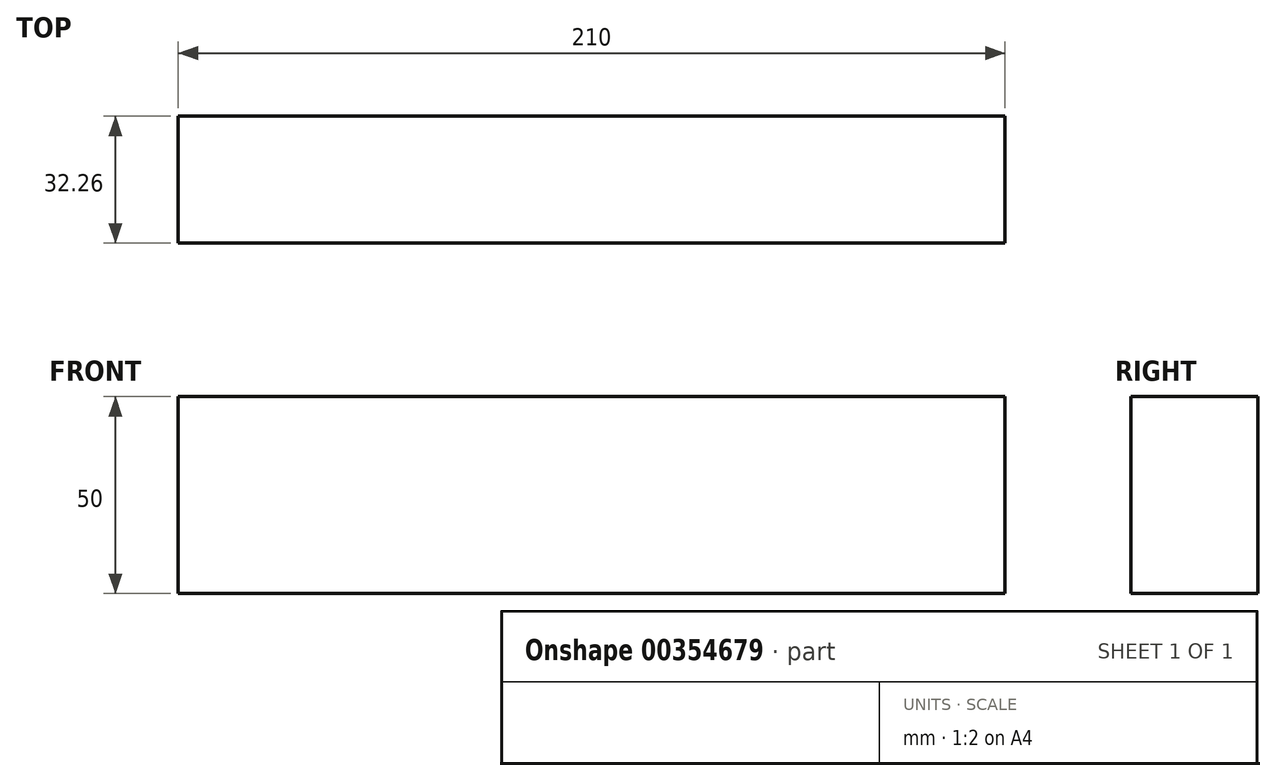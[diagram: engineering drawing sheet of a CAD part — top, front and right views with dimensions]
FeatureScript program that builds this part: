
annotation { "Feature Type Name" : "Feature", "Feature Type Description" : "" }
export const myFeature = defineFeature(function(context is Context, id is Id, definition is map)
    precondition{}
    {
        {
            var Q0;
            Q0=qCreatedBy(makeId("Front.planeOp"),FACE);
            var sketch = newSketch(context, id + "F0", { "sketchPlane" : qUnion([Q0])});
            skLineSegment(sketch, "E0.bottom", {"start": v(-105, 25) * mm, "end": v(105, 25) * mm});
            skLineSegment(sketch, "E0.top", {"start": v(-105, -25) * mm, "end": v(105, -25) * mm});
            skLineSegment(sketch, "E0.left", {"start": v(-105, 25) * mm, "end": v(-105, -25) * mm});
            skLineSegment(sketch, "E0.right", {"start": v(105, 25) * mm, "end": v(105, -25) * mm});
            skPoint(sketch, "E0.middle", {"position": v(0, 0) * mm});
            skSolve(sketch);
        }
        {
            var Q0;
            Q0=makeQuery(id+"F0.imprint","IMPRINT",FACE,{"disambiguationData":[TD([[makeQuery(id+"F0.imprint","IMPRINT",EDGE,{"derivedFrom":sQuery(id+"F0.wireOp",EDGE,"E0.bottom")}),-1.0]])]});
            extrude(context, id + "F1", {"entities" : qUnion([Q0]), "depth" : 32.26 * mm});
        }
    });
